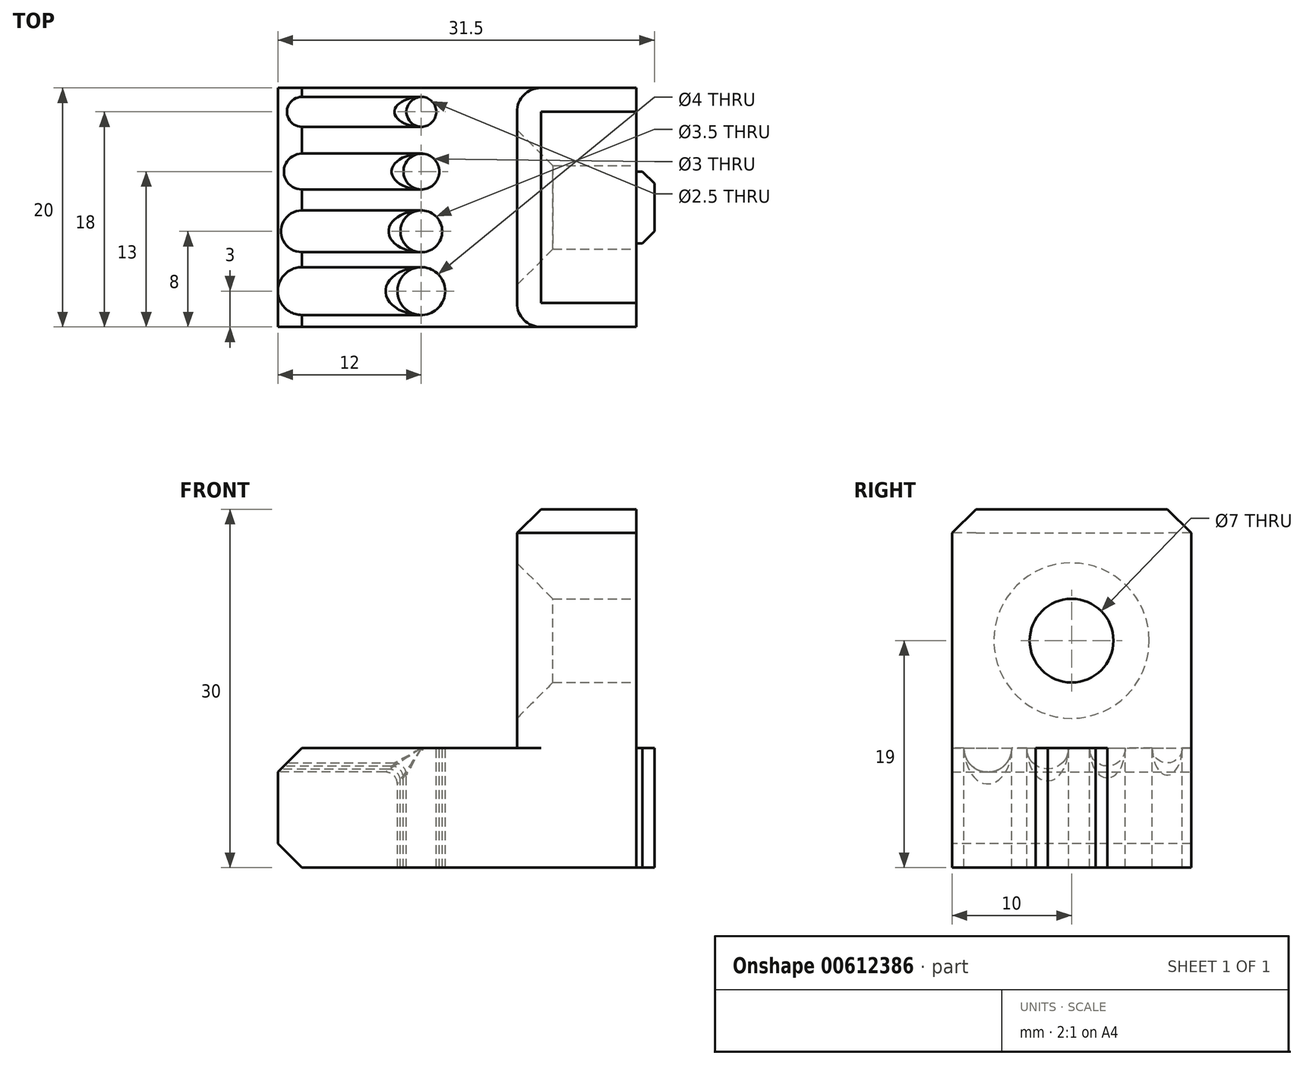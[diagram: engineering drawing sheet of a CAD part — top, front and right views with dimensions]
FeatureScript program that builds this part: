
annotation { "Feature Type Name" : "Feature", "Feature Type Description" : "" }
export const myFeature = defineFeature(function(context is Context, id is Id, definition is map)
    precondition{}
    {
        {
            var Q0;
            Q0=qCreatedBy(makeId("Top.planeOp"),FACE);
            var sketch = newSketch(context, id + "F0", { "sketchPlane" : qUnion([Q0])});
            skLineSegment(sketch, "E0.bottom", {"start": v(-5, 10) * mm, "end": v(5, 10) * mm});
            skLineSegment(sketch, "E0.top", {"start": v(-5, -10) * mm, "end": v(5, -10) * mm});
            skLineSegment(sketch, "E0.left", {"start": v(-5, 10) * mm, "end": v(-5, -10) * mm});
            skLineSegment(sketch, "E0.right", {"start": v(5, 10) * mm, "end": v(5, 3) * mm});
            skLineSegment(sketch, "E1.bottom", {"start": v(5, 3) * mm, "end": v(6.5, 3) * mm});
            skLineSegment(sketch, "E1.top", {"start": v(5, -3) * mm, "end": v(6.5, -3) * mm});
            skLineSegment(sketch, "E1.right", {"start": v(6.5, 3) * mm, "end": v(6.5, -3) * mm});
            skLineSegment(sketch, "E2.trimOffspring", {"start": v(5, -3) * mm, "end": v(5, -10) * mm});
            skSolve(sketch);
        }
        {
            var Q0;
            Q0=makeQuery(id+"F0.imprint","IMPRINT",FACE,{"disambiguationData":[TD([[makeQuery(id+"F0.imprint","IMPRINT",EDGE,{"derivedFrom":sQuery(id+"F0.wireOp",EDGE,"E0.bottom")}),-1.0]])]});
            extrude(context, id + "F1", {"entities" : qUnion([Q0]), "depth" : 30 * mm, "offsetDistance" : 25 * mm});
        }
        {
            var Q0;
            Q0=makeQuery(id+"F1.opExtrude","SWEPT_FACE",FACE,{"disambiguationData":[OSD([sQuery(id+"F0.wireOp",EDGE,"E1.right")])]});
            var sketch = newSketch(context, id + "F2", { "sketchPlane" : qUnion([Q0])});
            skCircle(sketch, "E3", {"center": v(0, 19) * mm, "radius": 3.5 * mm});
            skPoint(sketch, "E3.centerSnap0", {"position": v(3, 19) * mm});
            skSolve(sketch);
        }
        {
            var Q0;
            {var subQ0=sQuery(id+"F2.wireOp",EDGE,"E3");var subQ1=sQuery(id+"F0.wireOp",EDGE,"E1.right");var subQ2=makeQuery(id+"F2.imprint","INTERSECT",VERTEX,{"derivedFrom":[makeQuery(id+"F1.opExtrude","SWEPT_EDGE",EDGE,{"disambiguationData":[OSD([sQuery(id+"F0.wireOp",EDGE,"E1.bottom"),subQ1])]}),subQ0]});Q0=makeQuery(id+"F2.imprint","IMPRINT",FACE,{"disambiguationData":[TD([[makeQuery(id+"F2.imprint","IMPRINT",EDGE,{"disambiguationData":[TD([[subQ2,-1.0]])],"derivedFrom":subQ0}),1.0]])]});}
            var Q1;
            {var subQ0=sQuery(id+"F2.wireOp",EDGE,"E3");var subQ1=sQuery(id+"F0.wireOp",EDGE,"E1.right");var subQ2=makeQuery(id+"F1.opExtrude","SWEPT_EDGE",EDGE,{"disambiguationData":[OSD([sQuery(id+"F0.wireOp",EDGE,"E1.top"),subQ1])]});var subQ3=makeQuery(id+"F2.imprint","INTERSECT",VERTEX,{"disambiguationData":[OD(0.0)],"derivedFrom":[subQ2,subQ0]});Q1=makeQuery(id+"F2.imprint","IMPRINT",FACE,{"disambiguationData":[TD([[makeQuery(id+"F2.imprint","IMPRINT",EDGE,{"disambiguationData":[TD([[subQ3,1.0]])],"derivedFrom":subQ0}),1.0]])]});}
            var Q2;
            {var subQ0=sQuery(id+"F2.wireOp",EDGE,"E3");var subQ1=makeQuery(id+"F1.opExtrude","SWEPT_EDGE",EDGE,{"disambiguationData":[OSD([sQuery(id+"F0.wireOp",EDGE,"E1.top"),sQuery(id+"F0.wireOp",EDGE,"E1.right")])]});var subQ2=makeQuery(id+"F2.imprint","INTERSECT",VERTEX,{"disambiguationData":[OD(0.0)],"derivedFrom":[subQ1,subQ0]});Q2=makeQuery(id+"F2.imprint","IMPRINT",FACE,{"disambiguationData":[TD([[makeQuery(id+"F2.imprint","IMPRINT",EDGE,{"disambiguationData":[TD([[subQ2,-1.0]])],"derivedFrom":subQ0}),1.0]])]});}
            extrude(context, id + "F3", {"entities" : qUnion([Q0, Q1, Q2]), "operationType" : NewBodyOperationType.REMOVE, "oppositeDirection" : true, "depth" : 15 * mm, "offsetDistance" : 25 * mm});
        }
        {
            var Q0;
            Q0=makeQuery(id+"F3.boolean.opBoolean","INTERSECT",EDGE,{"derivedFrom":[makeQuery(id+"F1.opExtrude","SWEPT_FACE",FACE,{"disambiguationData":[OSD([sQuery(id+"F0.wireOp",EDGE,"E0.left")])]}),makeQuery(id+"F3.opExtrude","SWEPT_FACE",FACE,{"disambiguationData":[OSD([sQuery(id+"F2.wireOp",EDGE,"E3")])]})]});
            chamfer(context, id + "F4", {"entities" : qUnion([Q0]), "width" : 3 * mm, "tangentPropagation" : true});
        }
        {
            var Q0;
            Q0=makeQuery(id+"F1.opExtrude","SWEPT_FACE",FACE,{"disambiguationData":[OSD([sQuery(id+"F0.wireOp",EDGE,"E0.left")])]});
            var sketch = newSketch(context, id + "F5", { "sketchPlane" : qUnion([Q0])});
            skLineSegment(sketch, "E4.bottom", {"start": v(10, 0) * mm, "end": v(-10, 0) * mm});
            skLineSegment(sketch, "E4.top", {"start": v(10, 10) * mm, "end": v(-10, 10) * mm});
            skLineSegment(sketch, "E4.left", {"start": v(10, 0) * mm, "end": v(10, 10) * mm});
            skLineSegment(sketch, "E4.right", {"start": v(-10, 0) * mm, "end": v(-10, 10) * mm});
            skSolve(sketch);
        }
        {
            var Q0;
            Q0=makeQuery(id+"F5.imprint","IMPRINT",FACE,{"disambiguationData":[TD([[makeQuery(id+"F5.imprint","IMPRINT",EDGE,{"derivedFrom":sQuery(id+"F5.wireOp",EDGE,"E4.bottom")}),-1.0]])]});
            var Q1;
            Q1=makeQuery(id+"F5.imprint","IMPRINT",FACE,{"disambiguationData":[TD([[makeQuery(id+"F5.imprint","IMPRINT",EDGE,{"derivedFrom":sQuery(id+"F5.wireOp",EDGE,"IIFBrSvH-ee1S-mx0q-YNUM-Y27iXPpcrN0q.bottom")}),1.0]])]});
            var Q2;
            Q2=makeQuery(id+"F5.imprint","IMPRINT",FACE,{"disambiguationData":[TD([[makeQuery(id+"F5.imprint","IMPRINT",EDGE,{"derivedFrom":sQuery(id+"F5.wireOp",EDGE,"E4.bottom")}),1.0]])]});
            extrude(context, id + "F6", {"entities" : qUnion([Q0, Q1, Q2]), "operationType" : NewBodyOperationType.ADD, "depth" : 20 * mm, "offsetDistance" : 25 * mm});
        }
        {
            var Q0;
            Q0=makeQuery(id+"F1.opExtrude","SWEPT_EDGE",EDGE,{"disambiguationData":[OSD([sQuery(id+"F0.wireOp",EDGE,"E0.top"),sQuery(id+"F0.wireOp",EDGE,"E0.left")])]});
            var Q1;
            Q1=makeQuery(id+"F1.opExtrude","SWEPT_EDGE",EDGE,{"disambiguationData":[OSD([sQuery(id+"F0.wireOp",EDGE,"E0.bottom"),sQuery(id+"F0.wireOp",EDGE,"E0.left")])]});
            fillet(context, id + "F7", {"entities" : qUnion([Q0, Q1]), "radius" : 2 * mm, "tangentPropagation" : true, "allowEdgeOverflow" : false});
        }
        {
            var Q0;
            Q0=makeQuery(id+"F6.opExtrude","CAP_EDGE",EDGE,{"disambiguationData":[OSD([sQuery(id+"F5.wireOp",EDGE,"E4.top")])],"isStart":false});
            var Q1;
            Q1=makeQuery(id+"F6.opExtrude","CAP_EDGE",EDGE,{"disambiguationData":[OSD([sQuery(id+"F5.wireOp",EDGE,"IIFBrSvH-ee1S-mx0q-YNUM-Y27iXPpcrN0q.top")])],"isStart":false});
            var Q2;
            Q2=makeQuery(id+"F6.opExtrude","CAP_EDGE",EDGE,{"disambiguationData":[OSD([sQuery(id+"F5.wireOp",EDGE,"IIFBrSvH-ee1S-mx0q-YNUM-Y27iXPpcrN0q.bottom")])],"isStart":false});
            var Q3;
            Q3=makeQuery(id+"F6.opExtrude","CAP_EDGE",EDGE,{"disambiguationData":[OSD([sQuery(id+"F5.wireOp",EDGE,"E4.bottom")])],"isStart":false});
            var Q4;
            Q4=makeQuery(id+"F1.opExtrude","CAP_EDGE",EDGE,{"disambiguationData":[OSD([sQuery(id+"F0.wireOp",EDGE,"E0.left")])],"isStart":true});
            var Q5;
            Q5=makeQuery(id+"F1.opExtrude","CAP_EDGE",EDGE,{"disambiguationData":[OSD([sQuery(id+"F0.wireOp",EDGE,"E0.left")])],"isStart":false});
            chamfer(context, id + "F8", {"entities" : qUnion([Q0, Q1, Q2, Q3, Q4, Q5]), "width" : 2 * mm, "tangentPropagation" : true});
        }
        {
            var Q0;
            Q0=makeQuery(id+"F6.opExtrude","SWEPT_FACE",FACE,{"disambiguationData":[OSD([sQuery(id+"F5.wireOp",EDGE,"E4.top")])]});
            var sketch = newSketch(context, id + "F9", { "sketchPlane" : qUnion([Q0])});
            skCircle(sketch, "E5", {"center": v(-13, 8) * mm, "radius": 1.25 * mm});
            skPoint(sketch, "E5.centerSnap0", {"position": v(-13, 10) * mm});
            skCircle(sketch, "E6", {"center": v(-13, 3) * mm, "radius": 1.5 * mm});
            skCircle(sketch, "E7", {"center": v(-13, -2) * mm, "radius": 1.75 * mm});
            skCircle(sketch, "E8", {"center": v(-13, -7) * mm, "radius": 2 * mm});
            skSolve(sketch);
        }
        {
            var Q0;
            Q0=makeQuery(id+"F9.imprint","IMPRINT",FACE,{"disambiguationData":[TD([[makeQuery(id+"F9.imprint","IMPRINT",EDGE,{"derivedFrom":sQuery(id+"F9.wireOp",EDGE,"E5")}),1.0]])]});
            var Q1;
            Q1=makeQuery(id+"F9.imprint","IMPRINT",FACE,{"disambiguationData":[TD([[makeQuery(id+"F9.imprint","IMPRINT",EDGE,{"derivedFrom":sQuery(id+"F9.wireOp",EDGE,"E6")}),1.0]])]});
            var Q2;
            Q2=makeQuery(id+"F9.imprint","IMPRINT",FACE,{"disambiguationData":[TD([[makeQuery(id+"F9.imprint","IMPRINT",EDGE,{"derivedFrom":sQuery(id+"F9.wireOp",EDGE,"E7")}),1.0]])]});
            var Q3;
            Q3=makeQuery(id+"F9.imprint","IMPRINT",FACE,{"disambiguationData":[TD([[makeQuery(id+"F9.imprint","IMPRINT",EDGE,{"derivedFrom":sQuery(id+"F9.wireOp",EDGE,"E8")}),1.0]])]});
            extrude(context, id + "F10", {"entities" : qUnion([Q0, Q1, Q2, Q3]), "operationType" : NewBodyOperationType.REMOVE, "oppositeDirection" : true, "depth" : 25 * mm, "offsetDistance" : 25 * mm});
        }
        {
            var Q0;
            Q0=makeQuery(id+"F6.opExtrude","CAP_FACE",FACE,{"disambiguationData":[OSD([sQuery(id+"F5.wireOp",EDGE,"E4.bottom"),sQuery(id+"F5.wireOp",EDGE,"E4.top"),sQuery(id+"F5.wireOp",EDGE,"E4.left"),sQuery(id+"F5.wireOp",EDGE,"E4.right")])],"isStart":false});
            var sketch = newSketch(context, id + "F11", { "sketchPlane" : qUnion([Q0])});
            skCircle(sketch, "E9", {"center": v(-8, 10) * mm, "radius": 1.25 * mm});
            skCircle(sketch, "E10", {"center": v(-3, 10) * mm, "radius": 1.5 * mm});
            skCircle(sketch, "E11", {"center": v(2, 10) * mm, "radius": 1.75 * mm});
            skCircle(sketch, "E12", {"center": v(7, 10) * mm, "radius": 2 * mm});
            skSolve(sketch);
        }
        {
            var Q0;
            Q0=makeQuery(id+"F11.imprint","IMPRINT",FACE,{"disambiguationData":[TD([[makeQuery(id+"F11.imprint","IMPRINT",EDGE,{"derivedFrom":sQuery(id+"F11.wireOp",EDGE,"E9")}),1.0]])]});
            var Q1;
            Q1=makeQuery(id+"F11.imprint","IMPRINT",FACE,{"disambiguationData":[TD([[makeQuery(id+"F11.imprint","IMPRINT",EDGE,{"derivedFrom":sQuery(id+"F11.wireOp",EDGE,"E10")}),1.0]])]});
            var Q2;
            Q2=makeQuery(id+"F11.imprint","IMPRINT",FACE,{"disambiguationData":[TD([[makeQuery(id+"F11.imprint","IMPRINT",EDGE,{"derivedFrom":sQuery(id+"F11.wireOp",EDGE,"E11")}),1.0]])]});
            var Q3;
            Q3=makeQuery(id+"F11.imprint","IMPRINT",FACE,{"disambiguationData":[TD([[makeQuery(id+"F11.imprint","IMPRINT",EDGE,{"derivedFrom":sQuery(id+"F11.wireOp",EDGE,"E12")}),1.0]])]});
            extrude(context, id + "F12", {"entities" : qUnion([Q0, Q1, Q2, Q3]), "operationType" : NewBodyOperationType.REMOVE, "oppositeDirection" : true, "depth" : 12.1 * mm, "offsetDistance" : 25 * mm});
        }
        {
            var Q0;
            Q0=makeQuery(id+"F12.boolean.opBoolean","INTERSECT",EDGE,{"disambiguationData":[OD(0.0)],"derivedFrom":[makeQuery(id+"F10.boolean.opBoolean","COPY",FACE,{"derivedFrom":makeQuery(id+"F10.opExtrude","SWEPT_FACE",FACE,{"disambiguationData":[OSD([sQuery(id+"F9.wireOp",EDGE,"E5")])]})}),makeQuery(id+"F12.opExtrude","SWEPT_FACE",FACE,{"disambiguationData":[OSD([sQuery(id+"F11.wireOp",EDGE,"E9")])]})]});
            var Q1;
            Q1=makeQuery(id+"F12.boolean.opBoolean","INTERSECT",EDGE,{"disambiguationData":[OD(0.0)],"derivedFrom":[makeQuery(id+"F10.boolean.opBoolean","COPY",FACE,{"derivedFrom":makeQuery(id+"F10.opExtrude","SWEPT_FACE",FACE,{"disambiguationData":[OSD([sQuery(id+"F9.wireOp",EDGE,"E6")])]})}),makeQuery(id+"F12.opExtrude","SWEPT_FACE",FACE,{"disambiguationData":[OSD([sQuery(id+"F11.wireOp",EDGE,"E10")])]})]});
            var Q2;
            Q2=makeQuery(id+"F12.boolean.opBoolean","INTERSECT",EDGE,{"disambiguationData":[OD(0.0)],"derivedFrom":[makeQuery(id+"F10.boolean.opBoolean","COPY",FACE,{"derivedFrom":makeQuery(id+"F10.opExtrude","SWEPT_FACE",FACE,{"disambiguationData":[OSD([sQuery(id+"F9.wireOp",EDGE,"E7")])]})}),makeQuery(id+"F12.opExtrude","SWEPT_FACE",FACE,{"disambiguationData":[OSD([sQuery(id+"F11.wireOp",EDGE,"E11")])]})]});
            var Q3;
            Q3=makeQuery(id+"F12.boolean.opBoolean","INTERSECT",EDGE,{"disambiguationData":[OD(0.0)],"derivedFrom":[makeQuery(id+"F10.boolean.opBoolean","COPY",FACE,{"derivedFrom":makeQuery(id+"F10.opExtrude","SWEPT_FACE",FACE,{"disambiguationData":[OSD([sQuery(id+"F9.wireOp",EDGE,"E8")])]})}),makeQuery(id+"F12.opExtrude","SWEPT_FACE",FACE,{"disambiguationData":[OSD([sQuery(id+"F11.wireOp",EDGE,"E12")])]})]});
            fillet(context, id + "F13", {"entities" : qUnion([Q0, Q1, Q2, Q3]), "radius" : 1 * mm, "tangentPropagation" : true, "allowEdgeOverflow" : false});
        }
        {
            var Q0;
            {var subQ0=sQuery(id+"F0.wireOp",EDGE,"E1.right");var subQ1=sQuery(id+"F0.wireOp",EDGE,"E1.top");Q0=makeQuery(id+"F3.boolean.opBoolean","SPLIT",EDGE,{"disambiguationData":[TD([makeQuery(id+"F1.opExtrude","CAP_FACE",FACE,{"disambiguationData":[OSD([sQuery(id+"F0.wireOp",EDGE,"E0.bottom"),sQuery(id+"F0.wireOp",EDGE,"E0.top"),sQuery(id+"F0.wireOp",EDGE,"E0.left"),sQuery(id+"F0.wireOp",EDGE,"E0.right"),sQuery(id+"F0.wireOp",EDGE,"E1.bottom"),subQ1,subQ0,sQuery(id+"F0.wireOp",EDGE,"E2.trimOffspring")])],"isStart":true})])],"derivedFrom":makeQuery(id+"F1.opExtrude","SWEPT_EDGE",EDGE,{"disambiguationData":[OSD([subQ1,subQ0])]})});}
            var Q1;
            {var subQ0=sQuery(id+"F0.wireOp",EDGE,"E1.right");var subQ1=sQuery(id+"F0.wireOp",EDGE,"E1.top");Q1=makeQuery(id+"F3.boolean.opBoolean","SPLIT",EDGE,{"disambiguationData":[TD([makeQuery(id+"F1.opExtrude","CAP_FACE",FACE,{"disambiguationData":[OSD([sQuery(id+"F0.wireOp",EDGE,"E0.bottom"),sQuery(id+"F0.wireOp",EDGE,"E0.top"),sQuery(id+"F0.wireOp",EDGE,"E0.left"),sQuery(id+"F0.wireOp",EDGE,"E0.right"),sQuery(id+"F0.wireOp",EDGE,"E1.bottom"),subQ1,subQ0,sQuery(id+"F0.wireOp",EDGE,"E2.trimOffspring")])],"isStart":false})])],"derivedFrom":makeQuery(id+"F1.opExtrude","SWEPT_EDGE",EDGE,{"disambiguationData":[OSD([subQ1,subQ0])]})});}
            var Q2;
            {var subQ0=sQuery(id+"F0.wireOp",EDGE,"E1.right");var subQ1=sQuery(id+"F0.wireOp",EDGE,"E1.bottom");Q2=makeQuery(id+"F3.boolean.opBoolean","SPLIT",EDGE,{"disambiguationData":[TD([makeQuery(id+"F1.opExtrude","CAP_FACE",FACE,{"disambiguationData":[OSD([sQuery(id+"F0.wireOp",EDGE,"E0.bottom"),sQuery(id+"F0.wireOp",EDGE,"E0.top"),sQuery(id+"F0.wireOp",EDGE,"E0.left"),sQuery(id+"F0.wireOp",EDGE,"E0.right"),subQ1,sQuery(id+"F0.wireOp",EDGE,"E1.top"),subQ0,sQuery(id+"F0.wireOp",EDGE,"E2.trimOffspring")])],"isStart":false})])],"derivedFrom":makeQuery(id+"F1.opExtrude","SWEPT_EDGE",EDGE,{"disambiguationData":[OSD([subQ1,subQ0])]})});}
            var Q3;
            {var subQ0=sQuery(id+"F0.wireOp",EDGE,"E1.right");var subQ1=sQuery(id+"F0.wireOp",EDGE,"E1.bottom");Q3=makeQuery(id+"F3.boolean.opBoolean","SPLIT",EDGE,{"disambiguationData":[TD([makeQuery(id+"F1.opExtrude","CAP_FACE",FACE,{"disambiguationData":[OSD([sQuery(id+"F0.wireOp",EDGE,"E0.bottom"),sQuery(id+"F0.wireOp",EDGE,"E0.top"),sQuery(id+"F0.wireOp",EDGE,"E0.left"),sQuery(id+"F0.wireOp",EDGE,"E0.right"),subQ1,sQuery(id+"F0.wireOp",EDGE,"E1.top"),subQ0,sQuery(id+"F0.wireOp",EDGE,"E2.trimOffspring")])],"isStart":true})])],"derivedFrom":makeQuery(id+"F1.opExtrude","SWEPT_EDGE",EDGE,{"disambiguationData":[OSD([subQ1,subQ0])]})});}
            chamfer(context, id + "F14", {"entities" : qUnion([Q0, Q1, Q2, Q3]), "width" : 1 * mm, "tangentPropagation" : true});
        }
        {
            var Q0;
            Q0=makeQuery(id+"F1.opExtrude","CAP_FACE",FACE,{"disambiguationData":[OSD([sQuery(id+"F0.wireOp",EDGE,"E0.bottom"),sQuery(id+"F0.wireOp",EDGE,"E0.top"),sQuery(id+"F0.wireOp",EDGE,"E0.left"),sQuery(id+"F0.wireOp",EDGE,"E0.right"),sQuery(id+"F0.wireOp",EDGE,"E1.bottom"),sQuery(id+"F0.wireOp",EDGE,"E1.top"),sQuery(id+"F0.wireOp",EDGE,"E1.right"),sQuery(id+"F0.wireOp",EDGE,"E2.trimOffspring")])],"isStart":false});
            var sketch = newSketch(context, id + "F15", { "sketchPlane" : qUnion([Q0])});
            skLineSegment(sketch, "E13.bottom", {"start": v(5, -3) * mm, "end": v(6.5, -3) * mm});
            skLineSegment(sketch, "E13.top", {"start": v(5, 3) * mm, "end": v(6.5, 3) * mm});
            skLineSegment(sketch, "E13.left", {"start": v(5, -3) * mm, "end": v(5, 3) * mm});
            skLineSegment(sketch, "E13.right", {"start": v(6.5, -3) * mm, "end": v(6.5, 3) * mm});
            skSolve(sketch);
        }
        {
            var Q0;
            {var subQ12=sQuery(id+"F15.wireOp",EDGE,"E13.left");Q0=makeQuery(id+"F15.imprint","IMPRINT",FACE,{"disambiguationData":[TD([[makeQuery(id+"F15.imprint","IMPRINT",EDGE,{"derivedFrom":subQ12}),-1.0]])]});}
            extrude(context, id + "F16", {"entities" : qUnion([Q0]), "operationType" : NewBodyOperationType.REMOVE, "oppositeDirection" : true, "depth" : 20 * mm, "offsetDistance" : 25 * mm});
        }
    });
